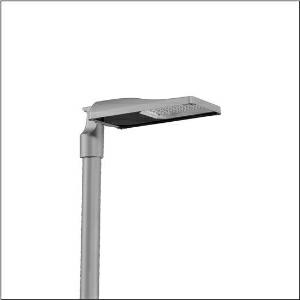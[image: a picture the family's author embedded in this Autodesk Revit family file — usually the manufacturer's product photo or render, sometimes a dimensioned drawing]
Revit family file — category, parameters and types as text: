
# Revit family: streetlight_sl_31_mini___st1_0a_5xh6d31a08ha_e135
name_source: partatom
category: Lighting Fixtures
units: mm (PartAtom-declared; Revit-internal decimal feet)

## family parameters
Cut with Voids When Loaded = No
Host = Face
Light Source = No
Part Type = Normal
Room Calculation Point = No
Round Connector Dimension = Use Diameter
Shared = No

## types (1)
- --- (1 x LED, 9240 lm, 68.3 W, 3000K)
    Apparent Load = 68 VA
    CIE Flux Codes = 37 72 97 100 100
    Color Rendering = 70
    Color Temperature = 3000K
    Default Elevation = 1800 mm
    Description = Streetlight SL 31 mini Easy, Desk-Remote mast luminaire for post-top, side-entry; light control with lens of PMMA; light distribution: ST1.0a, direct asymmetric distribution, for standard-compliant lighting for roads and squares; LED: luminous flux: 9.240lm, light colour: 730, colour temperature: 3000K; luminous efficacy: 135,3lm/W; control: pre-setting: linear dimming characteristic, flexible luminous flux parameterisation, time-dependent luminous flux control, constant luminous flux control, intelligent temperature release in ECG and LED module, overheat protection; luminaire housing, of diecast aluminium, Siteco® metallic grey (DB 702S), corrosivity category C5 high according to DIN EN ISO 12944; cover of toughened safety glass, transparent, opened without tools; mast flange of diecast aluminium, Siteco® metallic grey (DB 702S), spigot size: 76/60mm, mast flange included unmounted; with cable H07RN-F 2x 1.5mm², cable length: 8,5m, connection cable pre-assembled; mains connection: 220..240V, AC, 50/60Hz; power consumption (at start of service life): 68,3W / (at end of service life): 74,8W / (with reduced operation 50%): 29,7W; protection rating (complete): IP66; insulation class (complete): insulation class II (safety insulation); impact resistance: IK10; certification: CE, ENEC, ENEC+, VDE, UKCA; permissible operating ambient temperature for outdoor applications: -40..+50°C; packaging unit: 1 piece

Light Distribution: ST1.0a
    Height = 76 mm
    Lamp = 1 x LED
    Lamp Light Flux = 9240 lm
    Lamp Power = 68.3 W
    Lamp count = 1
    Length = 547 mm
    Luminous efficacy = 135 lm/W
    Manufacturer = Siteco
    ModVariant = No
    Model = 5XH6D31A08HA
    Number of Poles = 1
    OnlyDefault = Yes
    Power Factor = 1
    Product Name = Streetlight SL 31 mini | ST1.0a
    Product group = mast luminaire | pylon top
    ProductGroupID = 6100
    Protection Class = Protection class II
    Protection Degree = IP 66
    RLX_Detail_Level = 1
    RLX_Emergency_Light_Flux = 0 lm
    RLX_Emergency_Type = 0
    RLX_Emergency_Type_DB = No
    RlxData = <blob elided: 39605 chars, md5=2e9d4871>
    Socket = socket
    Standby Power = 0 W
    System Light Flux = 9240 lm
    System Power = 68 W
    Type Comments = factory setting: luminous flux: 100 % | dim-lin: 254 | 693 mA
    Type Image = l_1300326.jpg
    URL = http://relux.com
    VarID = @adj_074701
    Voltage = 0 V
    Weight = 0.00 kg
    Width = 265 mm

## geometry (parser evidence)
native form markers: Blend x4, Sweep x11
no freeform markers — native parametric forms only
